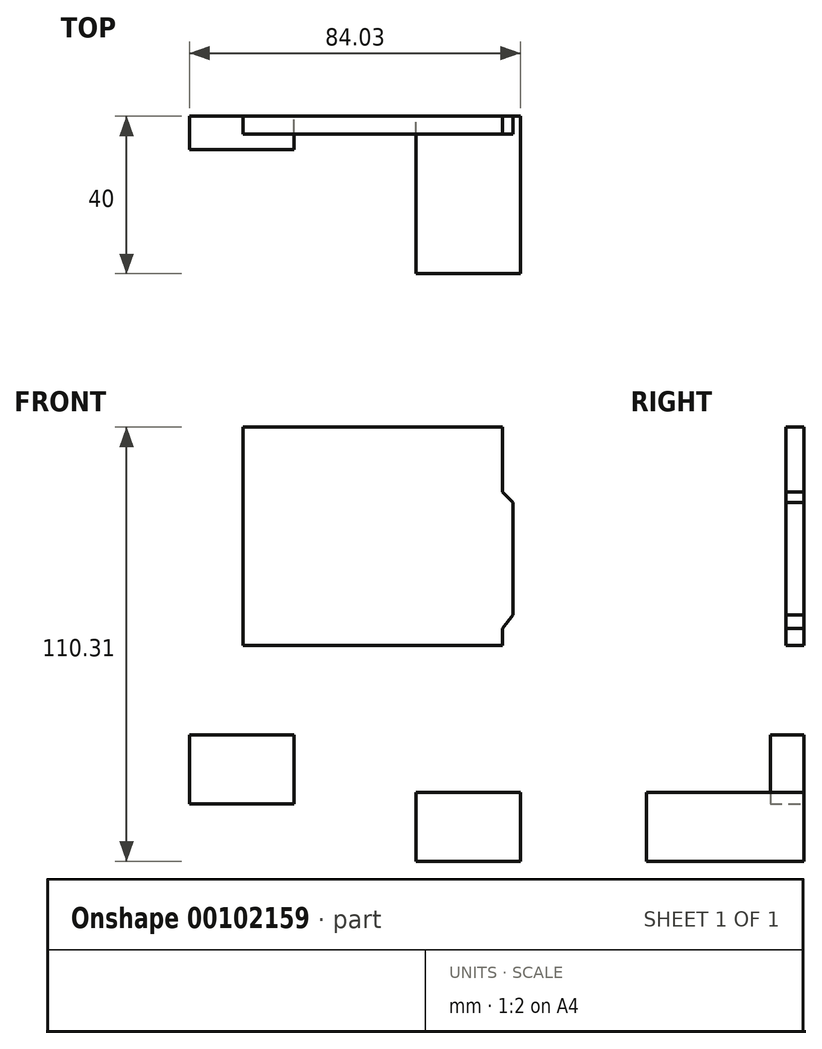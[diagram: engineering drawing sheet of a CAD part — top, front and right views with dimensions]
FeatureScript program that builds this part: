
annotation { "Feature Type Name" : "Feature", "Feature Type Description" : "" }
export const myFeature = defineFeature(function(context is Context, id is Id, definition is map)
    precondition{}
    {
        {
            var Q0;
            Q0=qCreatedBy(makeId("Front.planeOp"),FACE);
            var sketch = newSketch(context, id + "F0", { "sketchPlane" : qUnion([Q0])});
            skLineSegment(sketch, "E0", {"start": v(-48.3, 0) * mm, "end": v(17.7, 0) * mm});
            skLineSegment(sketch, "E1", {"start": v(17.7, 0) * mm, "end": v(17.7, 4.42) * mm});
            skLineSegment(sketch, "E2", {"start": v(17.7, 4.42) * mm, "end": v(20.28, 7.84) * mm});
            skLineSegment(sketch, "E3", {"start": v(20.28, 7.84) * mm, "end": v(20.28, 36.4) * mm});
            skLineSegment(sketch, "E4", {"start": v(20.28, 36.4) * mm, "end": v(17.7, 39.02) * mm});
            skLineSegment(sketch, "E5", {"start": v(17.7, 39.02) * mm, "end": v(17.7, 55.5) * mm});
            skLineSegment(sketch, "E6", {"start": v(17.7, 55.5) * mm, "end": v(-48.3, 55.5) * mm});
            skLineSegment(sketch, "E7", {"start": v(-48.3, 55.5) * mm, "end": v(-48.3, 0) * mm});
            skSolve(sketch);
        }
        {
            var Q0;
            Q0 = qSketchRegion(id + "F0", true);
            extrude(context, id + "F1", {"entities" : qUnion([Q0]), "depth" : 4.54 * mm});
        }
        {
            var Q0;
            Q0=qCreatedBy(makeId("Front.planeOp"),FACE);
            var sketch = newSketch(context, id + "F2", { "sketchPlane" : qUnion([Q0])});
            skLineSegment(sketch, "E8.bottom", {"start": v(-4.28, -37.3) * mm, "end": v(22.22, -37.3) * mm});
            skLineSegment(sketch, "E8.top", {"start": v(-4.28, -54.8) * mm, "end": v(22.22, -54.8) * mm});
            skLineSegment(sketch, "E8.left", {"start": v(-4.28, -37.3) * mm, "end": v(-4.28, -54.8) * mm});
            skLineSegment(sketch, "E8.right", {"start": v(22.22, -37.3) * mm, "end": v(22.22, -54.8) * mm});
            skSolve(sketch);
        }
        {
            var Q0;
            Q0 = qSketchRegion(id + "F2", true);
            extrude(context, id + "F3", {"entities" : qUnion([Q0]), "depth" : 40 * mm});
        }
        {
            var Q0;
            Q0=qCreatedBy(makeId("Front.planeOp"),FACE);
            var sketch = newSketch(context, id + "F4", { "sketchPlane" : qUnion([Q0])});
            skLineSegment(sketch, "E9.bottom", {"start": v(-61.8, -22.69) * mm, "end": v(-35.3, -22.69) * mm});
            skLineSegment(sketch, "E9.top", {"start": v(-61.8, -40.19) * mm, "end": v(-35.3, -40.19) * mm});
            skLineSegment(sketch, "E9.left", {"start": v(-61.8, -22.69) * mm, "end": v(-61.8, -40.19) * mm});
            skLineSegment(sketch, "E9.right", {"start": v(-35.3, -22.69) * mm, "end": v(-35.3, -40.19) * mm});
            skSolve(sketch);
        }
        {
            var Q0;
            Q0 = qSketchRegion(id + "F4", true);
            extrude(context, id + "F5", {"entities" : qUnion([Q0]), "depth" : 8.5 * mm});
        }
    });
